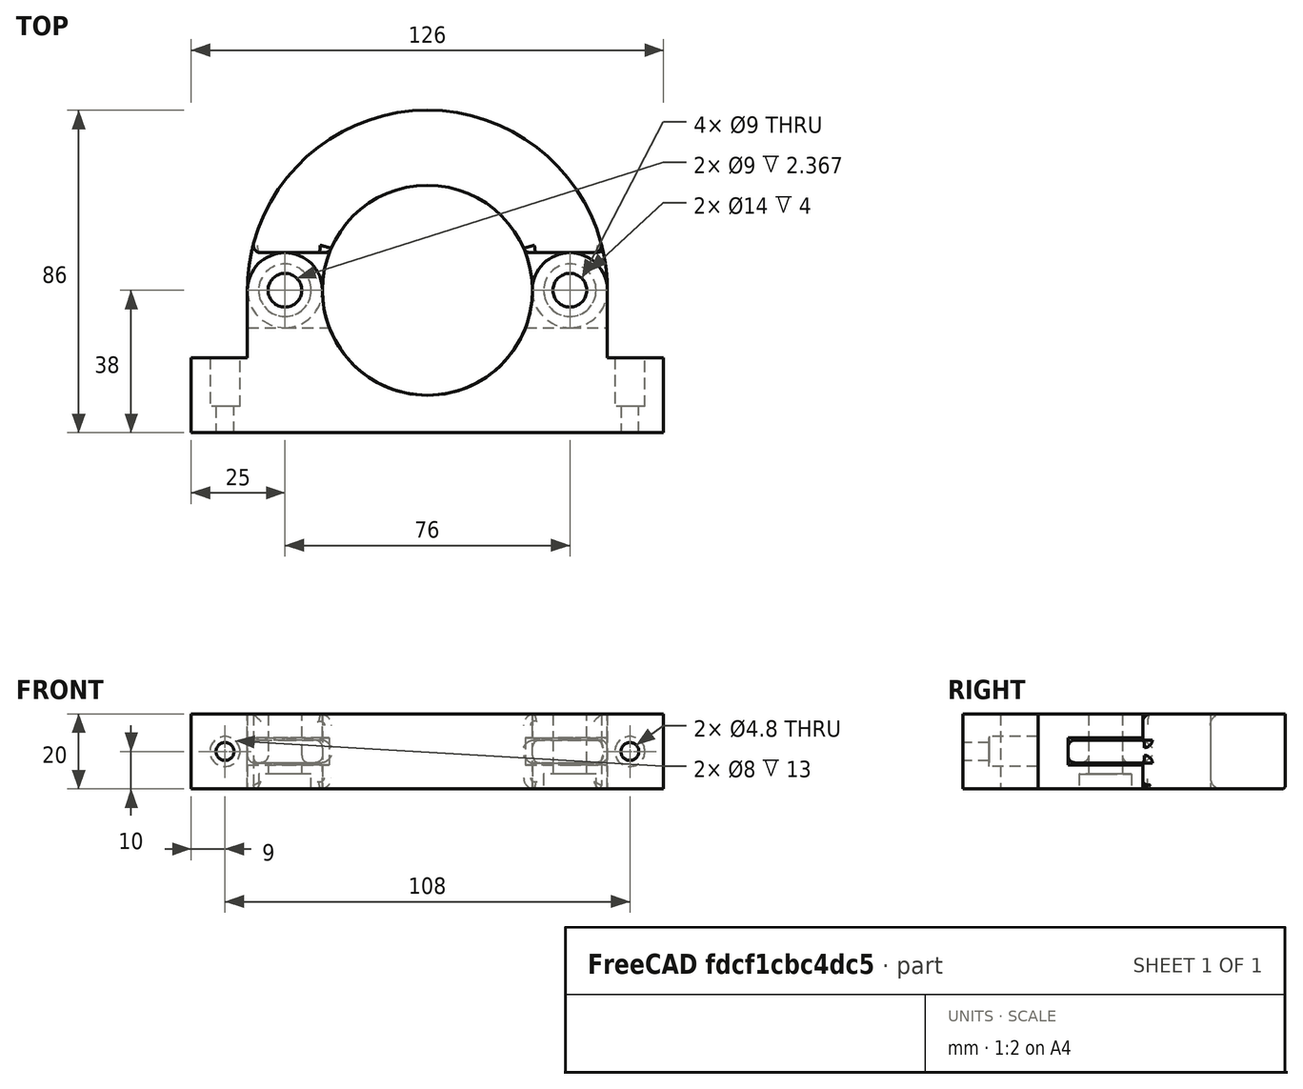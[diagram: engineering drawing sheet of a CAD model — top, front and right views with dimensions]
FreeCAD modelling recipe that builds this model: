
FCSTD DOCUMENT  (FreeCAD 1.0R1.0.0)
Label: ProfileMountClamp01
License: All rights reserved
LicenseURL: http://en.wikipedia.org/wiki/All_rights_reserved
objects: Part::Cylinder×26, Part::MultiFuse×13, Part::Box×9, Part::Cut×8, Part::Fillet×4, Spreadsheet::Sheet×1
note: 60 computed .brp shape members not serialized (recipe doc carries the construction recipe); baked Part::Feature solids carry a one-line shape summary decoded from their .brp

FEATURE [Spreadsheet::Sheet] Spreadsheet
  cells = A2='Inner diameter; B2(innerdia)=56; A3='Profile thickness; B3(profilethick)=20; A4='Wall width; B4(wallwidth)=20; A5='Spacing tolerance; B5(tolerance)=0.3
FEATURE [Part::Cylinder] Cylinder
  Angle = 360
  AttacherType = Attacher::AttachEngine3D
  FirstAngle = 0
  Height = 20
  Radius = 28
  SecondAngle = 0
  expr: Height = Spreadsheet.profilethick
  expr: Radius = Spreadsheet.innerdia / 2
FEATURE [Part::Box] Box  label="Cube"
  AttacherType = Attacher::AttachEngine3D
  Height = 20
  Length = 126
  Placement = pos=(-63,-38,0) rot=(0,0,1;0rad)
  Width = 20
  expr: .Placement.Base.x = -(<<Spreadsheet>>.innerdia + 2 * Spreadsheet.wallwidth + 30) / 2
  expr: .Placement.Base.y = -Spreadsheet.innerdia / 2 - Spreadsheet.profilethick / 2
  expr: .Placement.Base.z = 0
  expr: Height = Spreadsheet.profilethick
  expr: Length = <<Spreadsheet>>.innerdia + 2 * Spreadsheet.wallwidth + 30
  expr: Width = Spreadsheet.profilethick
FEATURE [Part::Box] Box001  label="Cube001"
  AttacherType = Attacher::AttachEngine3D
  Height = 20
  Length = 96
  Placement = pos=(-48,-28,0) rot=(0,0,1;0rad)
  Width = 28
  expr: .Placement.Base.x = -Spreadsheet.innerdia / 2 - Spreadsheet.wallwidth
  expr: .Placement.Base.y = -<<Spreadsheet>>.innerdia / 2
  expr: Height = Spreadsheet.profilethick
  expr: Length = Spreadsheet.innerdia + 2 * Spreadsheet.wallwidth
  expr: Width = Spreadsheet.innerdia / 2
FEATURE [Part::Cylinder] Cylinder001
  Angle = 360
  AttacherType = Attacher::AttachEngine3D
  FirstAngle = 0
  Height = 20
  Placement = pos=(38,0,0) rot=(0,0,1;0rad)
  Radius = 10
  SecondAngle = 0
  expr: .Placement.Base.x = Spreadsheet.innerdia / 2 + Spreadsheet.wallwidth / 2
  expr: Height = Spreadsheet.profilethick
  expr: Radius = Spreadsheet.wallwidth / 2
FEATURE [Part::Cylinder] Cylinder002
  Angle = 360
  AttacherType = Attacher::AttachEngine3D
  FirstAngle = 0
  Height = 20
  Placement = pos=(-38,0,0) rot=(0,0,1;0rad)
  Radius = 10
  SecondAngle = 0
  expr: .Placement.Base.x = -(Spreadsheet.innerdia / 2 + Spreadsheet.wallwidth / 2)
  expr: Height = Spreadsheet.profilethick
  expr: Radius = Spreadsheet.wallwidth / 2
FEATURE [Part::MultiFuse] Fusion
  Shapes = -> [Box,Box001,Cylinder001,Cylinder002]
FEATURE [Part::Cylinder] Cylinder003
  Angle = 360
  AttacherType = Attacher::AttachEngine3D
  FirstAngle = 0
  Height = 20
  Radius = 28
  SecondAngle = 0
  expr: Height = Spreadsheet.profilethick
  expr: Radius = Spreadsheet.innerdia / 2
FEATURE [Part::Cut] Cut
  Base = -> Fusion
  Tool = -> Cylinder
FEATURE [Part::Cylinder] Cylinder004
  Angle = 360
  AttacherType = Attacher::AttachEngine3D
  FirstAngle = 0
  Height = 11
  Radius = 2.4
  SecondAngle = 0
FEATURE [Part::Cylinder] Cylinder005
  Angle = 360
  AttacherType = Attacher::AttachEngine3D
  FirstAngle = 0
  Height = 100
  Placement = pos=(0,0,7) rot=(0,0,1;0rad)
  Radius = 4
  SecondAngle = 0
FEATURE [Part::MultiFuse] Fusion001
  Placement = pos=(54,-38,10) rot=(1,0,0;-1.5708rad)
  Shapes = -> [Cylinder005,Cylinder004]
  expr: .Placement.Base.x = (<<Spreadsheet>>.innerdia + 2 * Spreadsheet.wallwidth) / 2 + 10 - 4
  expr: .Placement.Base.y = -Spreadsheet.innerdia / 2 - Spreadsheet.profilethick / 2
  expr: .Placement.Base.z = Spreadsheet.profilethick / 2
FEATURE [Part::Cylinder] Cylinder006
  Angle = 360
  AttacherType = Attacher::AttachEngine3D
  FirstAngle = 0
  Height = 11
  Radius = 2.4
  SecondAngle = 0
FEATURE [Part::Cylinder] Cylinder007
  Angle = 360
  AttacherType = Attacher::AttachEngine3D
  FirstAngle = 0
  Height = 100
  Placement = pos=(0,0,7) rot=(0,0,1;0rad)
  Radius = 4
  SecondAngle = 0
FEATURE [Part::MultiFuse] Fusion002
  Placement = pos=(-54,-38,10) rot=(1,0,0;-1.5708rad)
  Shapes = -> [Cylinder007,Cylinder006]
  expr: .Placement.Base.x = -((<<Spreadsheet>>.innerdia + 2 * Spreadsheet.wallwidth) / 2 + 10 - 4)
  expr: .Placement.Base.y = -Spreadsheet.innerdia / 2 - Spreadsheet.profilethick / 2
  expr: .Placement.Base.z = Spreadsheet.profilethick / 2
FEATURE [Part::MultiFuse] Fusion003
  Shapes = -> [Fusion001,Fusion002]
FEATURE [Part::Cut] Cut001
  Base = -> Cut
  Tool = -> Fusion003
FEATURE [Part::Cylinder] Cylinder008
  Angle = 360
  AttacherType = Attacher::AttachEngine3D
  FirstAngle = 0
  Height = 7.26667
  Placement = pos=(38,0,6.36667) rot=(0,0,1;0rad)
  Radius = 10
  SecondAngle = 0
  expr: .Placement.Base.x = Spreadsheet.innerdia / 2 + Spreadsheet.wallwidth / 2
  expr: .Placement.Base.z = Spreadsheet.profilethick / 3 - Spreadsheet.tolerance
  expr: Height = Spreadsheet.profilethick / 3 + 2 * Spreadsheet.tolerance
  expr: Radius = Spreadsheet.wallwidth / 2
FEATURE [Part::Cylinder] Cylinder009
  Angle = 360
  AttacherType = Attacher::AttachEngine3D
  FirstAngle = 0
  Height = 7.26667
  Placement = pos=(-38,0,6.36667) rot=(0,0,1;0rad)
  Radius = 10
  SecondAngle = 0
  expr: .Placement.Base.x = -(Spreadsheet.innerdia / 2 + Spreadsheet.wallwidth / 2)
  expr: .Placement.Base.z = Spreadsheet.profilethick / 3 - Spreadsheet.tolerance
  expr: Height = Spreadsheet.profilethick / 3 + 2 * Spreadsheet.tolerance
  expr: Radius = Spreadsheet.wallwidth / 2
FEATURE [Part::Cylinder] Cylinder010
  Angle = 360
  AttacherType = Attacher::AttachEngine3D
  FirstAngle = 0
  Height = 20
  Placement = pos=(38,0,0) rot=(0,0,1;0rad)
  Radius = 4.5
  SecondAngle = 0
  expr: .Placement.Base.x = Spreadsheet.innerdia / 2 + Spreadsheet.wallwidth / 2
  expr: Height = Spreadsheet.profilethick
FEATURE [Part::Cylinder] Cylinder011
  Angle = 360
  AttacherType = Attacher::AttachEngine3D
  FirstAngle = 0
  Height = 4
  Placement = pos=(38,0,0) rot=(0,0,1;0rad)
  Radius = 7
  SecondAngle = 0
  expr: .Placement.Base.x = Spreadsheet.innerdia / 2 + Spreadsheet.wallwidth / 2
  expr: Height = 4
FEATURE [Part::MultiFuse] Fusion004
  Shapes = -> [Cylinder010,Cylinder011]
FEATURE [Part::Cylinder] Cylinder012
  Angle = 360
  AttacherType = Attacher::AttachEngine3D
  FirstAngle = 0
  Height = 20
  Placement = pos=(-38,0,0) rot=(0,0,1;0rad)
  Radius = 4.5
  SecondAngle = 0
  expr: .Placement.Base.x = -(Spreadsheet.innerdia / 2 + Spreadsheet.wallwidth / 2)
  expr: Height = Spreadsheet.profilethick
FEATURE [Part::Cylinder] Cylinder013
  Angle = 360
  AttacherType = Attacher::AttachEngine3D
  FirstAngle = 0
  Height = 4
  Placement = pos=(-38,0,0) rot=(0,0,1;0rad)
  Radius = 7
  SecondAngle = 0
  expr: .Placement.Base.x = -(Spreadsheet.innerdia / 2 + Spreadsheet.wallwidth / 2)
  expr: Height = 4
FEATURE [Part::MultiFuse] Fusion005
  Shapes = -> [Cylinder012,Cylinder013]
FEATURE [Part::Cylinder] Cylinder014
  Angle = 360
  AttacherType = Attacher::AttachEngine3D
  FirstAngle = 0
  Height = 20
  Radius = 28
  SecondAngle = 0
  expr: Height = Spreadsheet.profilethick
  expr: Radius = Spreadsheet.innerdia / 2
FEATURE [Part::Cylinder] Cylinder015
  Angle = 360
  AttacherType = Attacher::AttachEngine3D
  FirstAngle = 0
  Height = 20
  Placement = pos=(38,0,0) rot=(0,0,1;0rad)
  Radius = 10
  SecondAngle = 0
  expr: .Placement.Base.x = Spreadsheet.innerdia / 2 + Spreadsheet.wallwidth / 2
  expr: Height = Spreadsheet.profilethick
  expr: Radius = Spreadsheet.wallwidth / 2
FEATURE [Part::Cylinder] Cylinder016
  Angle = 360
  AttacherType = Attacher::AttachEngine3D
  FirstAngle = 0
  Height = 20
  Placement = pos=(-38,0,0) rot=(0,0,1;0rad)
  Radius = 10
  SecondAngle = 0
  expr: .Placement.Base.x = -(Spreadsheet.innerdia / 2 + Spreadsheet.wallwidth / 2)
  expr: Height = Spreadsheet.profilethick
  expr: Radius = Spreadsheet.wallwidth / 2
FEATURE [Part::Cylinder] Cylinder017
  Angle = 360
  AttacherType = Attacher::AttachEngine3D
  FirstAngle = 0
  Height = 20
  Radius = 48
  SecondAngle = 0
  expr: Height = Spreadsheet.profilethick
  expr: Radius = Spreadsheet.innerdia / 2 + Spreadsheet.wallwidth
FEATURE [Part::Cut] Cut003
  Base = -> Cylinder017
  Tool = -> Cylinder014
FEATURE [Part::Box] Box002  label="Cube002"
  AttacherType = Attacher::AttachEngine3D
  Height = 20
  Length = 96
  Placement = pos=(-48,-48,0) rot=(0,0,1;0rad)
  Width = 48
  expr: .Placement.Base.x = -(Spreadsheet.innerdia + 2 * Spreadsheet.wallwidth) / 2
  expr: .Placement.Base.y = -(Spreadsheet.innerdia + 2 * Spreadsheet.wallwidth) / 2
  expr: Height = Spreadsheet.profilethick
  expr: Length = Spreadsheet.innerdia + 2 * Spreadsheet.wallwidth
  expr: Width = (Spreadsheet.innerdia + 2 * Spreadsheet.wallwidth) / 2
FEATURE [Part::Cut] Cut004
  Base = -> Cut003
  Tool = -> Box002
FEATURE [Part::MultiFuse] Fusion007
  Shapes = -> [Cut004,Cylinder015,Cylinder016]
FEATURE [Part::Cylinder] Cylinder018
  Angle = 360
  AttacherType = Attacher::AttachEngine3D
  FirstAngle = 0
  Height = 20
  Placement = pos=(38,0,0) rot=(0,0,1;0rad)
  Radius = 4.5
  SecondAngle = 0
  expr: .Placement.Base.x = Spreadsheet.innerdia / 2 + Spreadsheet.wallwidth / 2
  expr: Height = Spreadsheet.profilethick
FEATURE [Part::Cylinder] Cylinder019
  Angle = 360
  AttacherType = Attacher::AttachEngine3D
  FirstAngle = 0
  Height = 4
  Placement = pos=(38,0,0) rot=(0,0,1;0rad)
  Radius = 7
  SecondAngle = 0
  expr: .Placement.Base.x = Spreadsheet.innerdia / 2 + Spreadsheet.wallwidth / 2
  expr: Height = 4
FEATURE [Part::Cylinder] Cylinder020
  Angle = 360
  AttacherType = Attacher::AttachEngine3D
  FirstAngle = 0
  Height = 20
  Placement = pos=(-38,0,0) rot=(0,0,1;0rad)
  Radius = 4.5
  SecondAngle = 0
  expr: .Placement.Base.x = -(Spreadsheet.innerdia / 2 + Spreadsheet.wallwidth / 2)
  expr: Height = Spreadsheet.profilethick
FEATURE [Part::Cylinder] Cylinder021
  Angle = 360
  AttacherType = Attacher::AttachEngine3D
  FirstAngle = 0
  Height = 4
  Placement = pos=(-38,0,0) rot=(0,0,1;0rad)
  Radius = 7
  SecondAngle = 0
  expr: .Placement.Base.x = -(Spreadsheet.innerdia / 2 + Spreadsheet.wallwidth / 2)
  expr: Height = 4
FEATURE [Part::MultiFuse] Fusion008
  Shapes = -> [Cylinder018,Cylinder019]
FEATURE [Part::MultiFuse] Fusion009
  Shapes = -> [Cylinder020,Cylinder021]
FEATURE [Part::MultiFuse] Fusion010
  Shapes = -> [Fusion009,Fusion008]
FEATURE [Part::Cut] Cut005  label="FusionWhatever"
  Base = -> Fusion007
  Tool = -> Fusion010
FEATURE [Part::Cylinder] Cylinder022
  Angle = 360
  AttacherType = Attacher::AttachEngine3D
  FirstAngle = 0
  Height = 6.96667
  Placement = pos=(38,0,0) rot=(0,0,1;0rad)
  Radius = 10
  SecondAngle = 0
  expr: .Placement.Base.x = Spreadsheet.innerdia / 2 + Spreadsheet.wallwidth / 2
  expr: Height = Spreadsheet.profilethick / 3 + Spreadsheet.tolerance
  expr: Radius = Spreadsheet.wallwidth / 2
FEATURE [Part::Cylinder] Cylinder024
  Angle = 360
  AttacherType = Attacher::AttachEngine3D
  FirstAngle = 0
  Height = 6.96667
  Placement = pos=(38,0,13.0333) rot=(0,0,1;0rad)
  Radius = 10
  SecondAngle = 0
  expr: .Placement.Base.x = Spreadsheet.innerdia / 2 + Spreadsheet.wallwidth / 2
  expr: .Placement.Base.z = Spreadsheet.profilethick - (Spreadsheet.profilethick / 3 + Spreadsheet.tolerance)
  expr: Height = Spreadsheet.profilethick / 3 + Spreadsheet.tolerance
  expr: Radius = Spreadsheet.wallwidth / 2
FEATURE [Part::Cylinder] Cylinder025
  Angle = 360
  AttacherType = Attacher::AttachEngine3D
  FirstAngle = 0
  Height = 6.96667
  Placement = pos=(-38,0,0) rot=(0,0,1;0rad)
  Radius = 10
  SecondAngle = 0
  expr: .Placement.Base.x = -(Spreadsheet.innerdia / 2 + Spreadsheet.wallwidth / 2)
  expr: Height = Spreadsheet.profilethick / 3 + Spreadsheet.tolerance
  expr: Radius = Spreadsheet.wallwidth / 2
FEATURE [Part::Cylinder] Cylinder026
  Angle = 360
  AttacherType = Attacher::AttachEngine3D
  FirstAngle = 0
  Height = 6.96667
  Placement = pos=(-38,0,13.0333) rot=(0,0,1;0rad)
  Radius = 10
  SecondAngle = 0
  expr: .Placement.Base.x = -(Spreadsheet.innerdia / 2 + Spreadsheet.wallwidth / 2)
  expr: .Placement.Base.z = Spreadsheet.profilethick - (Spreadsheet.profilethick / 3 + Spreadsheet.tolerance)
  expr: Height = Spreadsheet.profilethick / 3 + Spreadsheet.tolerance
  expr: Radius = Spreadsheet.wallwidth / 2
FEATURE [Part::MultiFuse] Fusion011
  Shapes = -> [Cylinder022,Cylinder024,Cylinder025,Cylinder026]
FEATURE [Part::Cut] Cut006
  Base = -> Cut005
  Tool = -> Fusion011
FEATURE [Part::Box] Box005  label="Cube005"
  AttacherType = Attacher::AttachEngine3D
  Height = 6.96667
  Length = 40
  Placement = pos=(-48,-10,0) rot=(0,0,1;0rad)
  Width = 20
  expr: .Placement.Base.x = -Spreadsheet.innerdia / 2 - Spreadsheet.wallwidth
  expr: .Placement.Base.y = -Spreadsheet.wallwidth / 2
  expr: Height = Spreadsheet.profilethick / 3 + Spreadsheet.tolerance
  expr: Length = 2 * Spreadsheet.wallwidth
  expr: Width = Spreadsheet.wallwidth
FEATURE [Part::Box] Box006  label="Cube006"
  AttacherType = Attacher::AttachEngine3D
  Height = 6.96667
  Length = 40
  Placement = pos=(-48,-10,13.0333) rot=(0,0,1;0rad)
  Width = 20
  expr: .Placement.Base.x = -Spreadsheet.innerdia / 2 - Spreadsheet.wallwidth
  expr: .Placement.Base.y = -Spreadsheet.wallwidth / 2
  expr: .Placement.Base.z = Spreadsheet.profilethick - (Spreadsheet.profilethick / 3 + Spreadsheet.tolerance)
  expr: Height = Spreadsheet.profilethick / 3 + Spreadsheet.tolerance
  expr: Length = 2 * Spreadsheet.wallwidth
  expr: Width = Spreadsheet.wallwidth
FEATURE [Part::Box] Box007  label="Cube007"
  AttacherType = Attacher::AttachEngine3D
  Height = 6.96667
  Length = 40
  Placement = pos=(18,-10,0) rot=(0,0,1;0rad)
  Width = 20
  expr: .Placement.Base.x = Spreadsheet.innerdia / 2 - Spreadsheet.wallwidth / 2
  expr: .Placement.Base.y = -Spreadsheet.wallwidth / 2
  expr: Height = Spreadsheet.profilethick / 3 + Spreadsheet.tolerance
  expr: Length = 2 * Spreadsheet.wallwidth
  expr: Width = Spreadsheet.wallwidth
FEATURE [Part::Box] Box008  label="Cube008"
  AttacherType = Attacher::AttachEngine3D
  Height = 6.96667
  Length = 40
  Placement = pos=(18,-10,13.0333) rot=(0,0,1;0rad)
  Width = 20
  expr: .Placement.Base.x = Spreadsheet.innerdia / 2 - Spreadsheet.wallwidth / 2
  expr: .Placement.Base.y = -Spreadsheet.wallwidth / 2
  expr: .Placement.Base.z = Spreadsheet.profilethick - (Spreadsheet.profilethick / 3 + Spreadsheet.tolerance)
  expr: Height = Spreadsheet.profilethick / 3 + Spreadsheet.tolerance
  expr: Length = 2 * Spreadsheet.wallwidth
  expr: Width = Spreadsheet.wallwidth
FEATURE [Part::MultiFuse] Fusion012
  Shapes = -> [Box005,Box006,Box007,Box008]
FEATURE [Part::Cut] Cut007
  Base = -> Cut006
  Tool = -> Fusion012
FEATURE [Part::Fillet] Fillet003
  Base = -> Cut007
  EdgeLinks = -> Cut007 [Edge1,Edge12]
  Edges = 2 edges r=3: [Edge1,Edge12]
FEATURE [Part::Fillet] Fillet004
  Base = -> Fillet003
  EdgeLinks = -> Fillet003 [Edge1,Edge3,Edge4,Edge6,Edge7,Edge9,Edge11,Edge14,Edge16,Edge18,Edge20,Edge21,Edge23,Edge24,Edge26,Edge27,Edge29,Edge31,Edge32,Edge34,Edge35,Edge37,Edge41,Edge42,Edge43,Edge44,Edge48,Edge49,Edge51,Edge52,Edge55,Edge56,Edge57,Edge58,Edge59,Edge63,Edge66]
  Edges = 37 edges r=2: [Edge1,Edge3,Edge4,Edge6,Edge7,Edge9,Edge11,Edge14,Edge16,Edge18,Edge20,Edge21,Edge23,Edge24,Edge26,Edge27,Edge29,Edge31,Edge32,Edge34,Edge35,Edge37,Edge41,Edge42,Edge43,Edge44,Edge48,Edge49,Edge51,Edge52,Edge55,Edge56,Edge57,Edge58,Edge59,Edge63,Edge66]
FEATURE [Part::Fillet] Fillet005
  Base = -> Fillet004
  EdgeLinks = -> Fillet004 [Edge8,Edge42]
  Edges = 2 edges r=1: [Edge8,Edge42]
FEATURE [Part::Fillet] Fillet006  label="UpperWithfilet"
  Base = -> Fillet005
  EdgeLinks = -> Fillet005 [Edge159,Edge164,Edge173,Edge176]
  Edges = 4 edges r=2: [Edge159,Edge164,Edge173,Edge176]
FEATURE [Part::Box] Box009  label="Cube009"
  AttacherType = Attacher::AttachEngine3D
  Height = 7.26667
  Length = 40
  Placement = pos=(18,-10,6.36667) rot=(0,0,1;0rad)
  Width = 20
  expr: .Placement.Base.x = Spreadsheet.innerdia / 2 - Spreadsheet.wallwidth / 2
  expr: .Placement.Base.y = -Spreadsheet.wallwidth / 2
  expr: .Placement.Base.z = Spreadsheet.profilethick / 3 - Spreadsheet.tolerance
  expr: Height = <<Spreadsheet>>.profilethick / 3 + 2 * Spreadsheet.tolerance
  expr: Length = Spreadsheet.wallwidth * 2
  expr: Width = <<Spreadsheet>>.wallwidth
FEATURE [Part::Box] Box010  label="Cube010"
  AttacherType = Attacher::AttachEngine3D
  Height = 7.26667
  Length = 40
  Placement = pos=(-58,-10,6.36667) rot=(0,0,1;0rad)
  Width = 20
  expr: .Placement.Base.x = -Spreadsheet.innerdia / 2 - 1.5 * Spreadsheet.wallwidth
  expr: .Placement.Base.y = -Spreadsheet.wallwidth / 2
  expr: .Placement.Base.z = Spreadsheet.profilethick / 3 - Spreadsheet.tolerance
  expr: Height = <<Spreadsheet>>.profilethick / 3 + 2 * Spreadsheet.tolerance
  expr: Length = Spreadsheet.wallwidth * 2
  expr: Width = <<Spreadsheet>>.wallwidth
FEATURE [Part::MultiFuse] Fusion006
  Shapes = -> [Cylinder008,Cylinder009,Fusion004,Fusion005,Box009,Box010]
FEATURE [Part::Cut] Cut002  label="PartLowerNoFillet"
  Base = -> Cut001
  Tool = -> Fusion006
